# Revit family: Shower-Shower_Trim-KOHLER-Coralais-K-TS15611_1
name_source: partatom
category: Plumbing Fixtures
revit_build: Autodesk Revit 2017 (Build: 20160225_1515(x64)
units: mm (PartAtom-declared; Revit-internal decimal feet)

## family parameters
Cut with Voids When Loaded = No
Host = Face
OmniClass Number = 23.31.17.00
OmniClass Title = Showers
Part Type = Normal
Room Calculation Point = No
Round Connector Dimension = Use Diameter
Shared = No

## types (3) — shared parameters
ADA Compliant = No
Assembly Code = D2010700
CW Connection = No
Cold Water Inlet = Cold Water Inlet
Date Modified = 07/02/2020
Default Elevation = 42"
Drain Included = No
Finish = Kohler-Metal-CP-Polished_Chrome
HW Connection = Yes
Handle Clearance = 3 1/16"
Height = 6 1/2"
Hot Water Inlet = Hot Water Inlet
Length = 6 5/16"
Manufacturer = KOHLER Co.
Master Format 2014 = 22 42 23
Master Format 2014 Name = Residential Showers
Material = Premium Metal Construction
Pressure = 80.00 psi
Product Documentation Link = https://www.us.kohler.com
Product Name = Coralais
Product Page URL = http://www.us.kohler.com
Tempered Water Inlet = Tempered Water Inlet
URL = https://www.us.kohler.com
Vent Connection = No
Waste Connection = No
Waste Water Outlet = Waste Water Outlet
Width = 6 1/2"

## per-type parameters (varying)
| type | Description | Flow Rate | Model | Type | WaterSense Certified |
| 2.5 GPM,CP-Polished Chrome | Rite-Temp shower valve trim with lever handle and 2.5 gpm showerhead | 3 GPM | K-TS15611-4-CP | 1 | No |
| 1.75 GPM,CP-Polished Chrome | Rite-Temp shower valve trim with lever handle and 1.75 gpm showerhead | 2 GPM | K-TS15611-4G-CP | 2 | Yes |
| 1.5 GPM,CP-Polished Chrome | Rite-Temp shower valve trim with lever handle and 1.5 gpm showerhead | 2 GPM | K-TS15611-4H-CP | 3 | Yes |

## geometry (parser evidence)
native form markers: Sweep x9
no freeform markers — native parametric forms only
